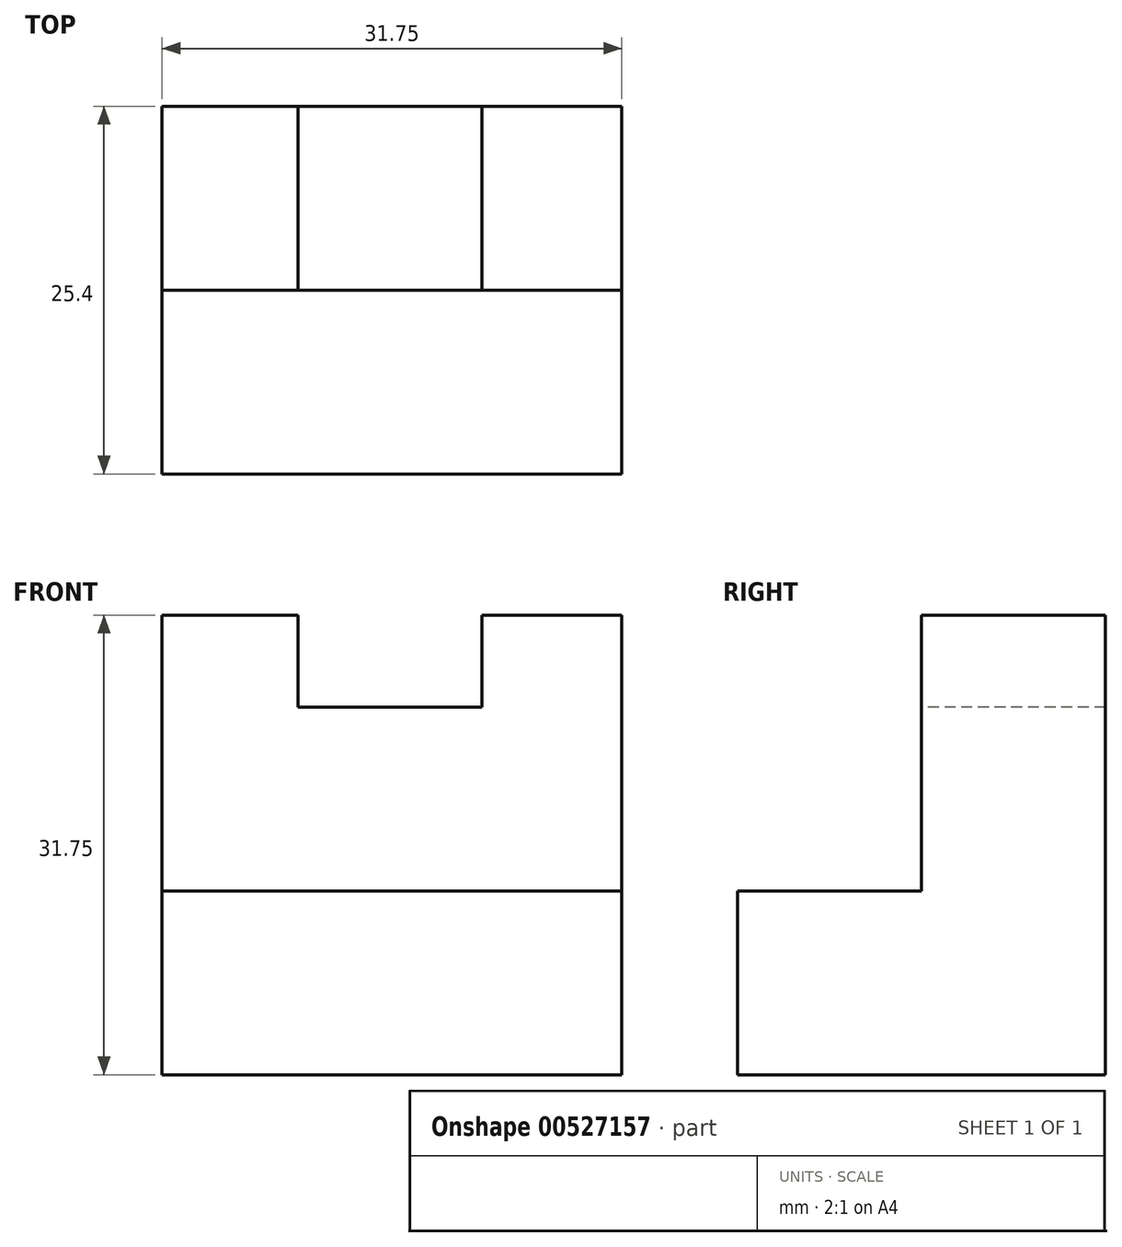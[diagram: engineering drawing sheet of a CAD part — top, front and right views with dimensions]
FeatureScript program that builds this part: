
annotation { "Feature Type Name" : "Feature", "Feature Type Description" : "" }
export const myFeature = defineFeature(function(context is Context, id is Id, definition is map)
    precondition{}
    {
        {
            var Q0;
            Q0=qCreatedBy(makeId("Right.planeOp"),FACE);
            var sketch = newSketch(context, id + "F0", { "sketchPlane" : qUnion([Q0])});
            skLineSegment(sketch, "E0", {"start": v(-12.7, 0) * mm, "end": v(-12.7, 19.05) * mm});
            skLineSegment(sketch, "E1", {"start": v(-12.7, 0) * mm, "end": v(-25.4, 0) * mm});
            skLineSegment(sketch, "E2", {"start": v(-25.4, 0) * mm, "end": v(-25.4, -12.7) * mm});
            skLineSegment(sketch, "E3", {"start": v(-25.4, -12.7) * mm, "end": v(0, -12.7) * mm});
            skLineSegment(sketch, "E4", {"start": v(0, -12.7) * mm, "end": v(0, 19.05) * mm});
            skLineSegment(sketch, "E5", {"start": v(-12.7, 19.05) * mm, "end": v(0, 19.05) * mm});
            skSolve(sketch);
        }
        {
            var Q0;
            Q0 = qSketchRegion(id + "F0", true);
            extrude(context, id + "F1", {"entities" : qUnion([Q0]), "depth" : 31.75 * mm, "offsetDistance" : 25.4 * mm});
        }
        {
            var Q0;
            Q0=makeQuery(id+"F1.opExtrude","SWEPT_FACE",FACE,{"disambiguationData":[OSD([sQuery(id+"F0.wireOp",EDGE,"E0")])]});
            var sketch = newSketch(context, id + "F2", { "sketchPlane" : qUnion([Q0])});
            skLineSegment(sketch, "E6", {"start": v(9.39, 19.05) * mm, "end": v(9.39, 12.7) * mm});
            skLineSegment(sketch, "E7", {"start": v(9.39, 12.7) * mm, "end": v(22.09, 12.7) * mm});
            skLineSegment(sketch, "E8", {"start": v(22.09, 12.7) * mm, "end": v(22.09, 19.05) * mm});
            skSolve(sketch);
        }
        {
            var Q0;
            Q0 = qSketchRegion(id + "F2", true);
            var Q1;
            {var subQ0=sQuery(id+"F2.wireOp",EDGE,"E6");Q1=makeQuery(id+"F2.imprint","IMPRINT",FACE,{"disambiguationData":[TD([[makeQuery(id+"F2.imprint","IMPRINT",EDGE,{"derivedFrom":subQ0}),1.0]])]});}
            extrude(context, id + "F3", {"entities" : qUnion([Q0, Q1]), "operationType" : NewBodyOperationType.REMOVE, "oppositeDirection" : true, "depth" : 25.4 * mm, "offsetDistance" : 25.4 * mm});
        }
    });
